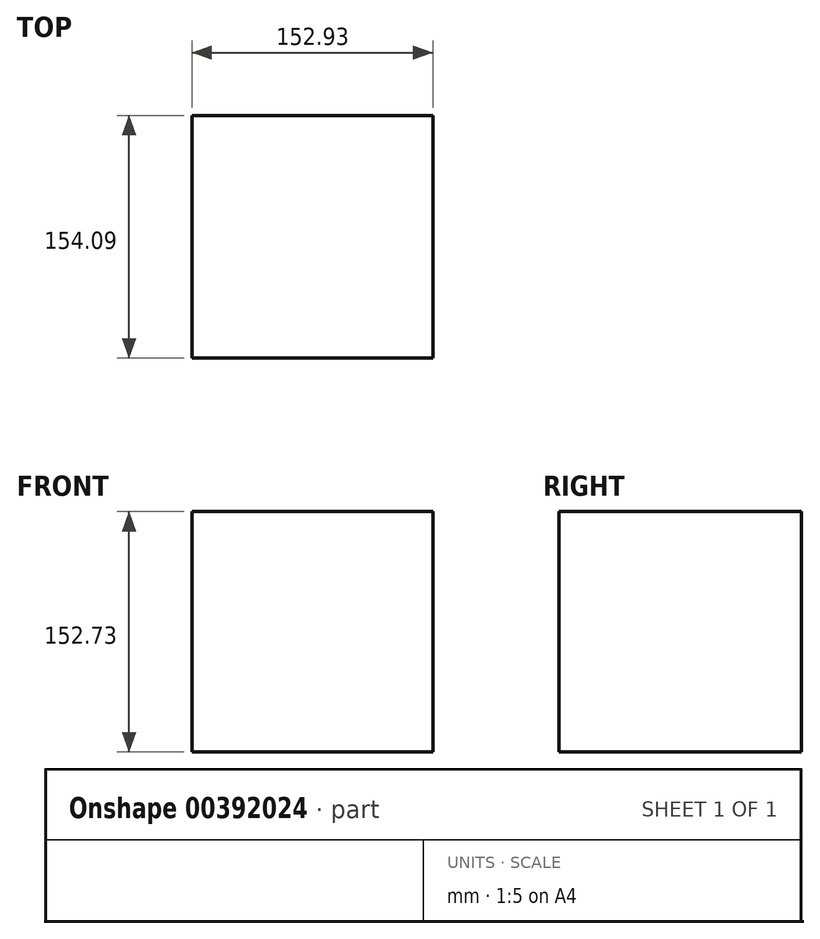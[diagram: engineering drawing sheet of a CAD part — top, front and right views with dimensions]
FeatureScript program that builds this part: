
annotation { "Feature Type Name" : "Feature", "Feature Type Description" : "" }
export const myFeature = defineFeature(function(context is Context, id is Id, definition is map)
    precondition{}
    {
        {
            var Q0;
            Q0=qCreatedBy(makeId("Front.planeOp"),FACE);
            var sketch = newSketch(context, id + "F0", { "sketchPlane" : qUnion([Q0])});
            skLineSegment(sketch, "E0.bottom", {"start": v(0, 0) * mm, "end": v(0, 0) * mm});
            skLineSegment(sketch, "E0.top", {"start": v(0, 0) * mm, "end": v(0, 0) * mm});
            skLineSegment(sketch, "E0.left", {"start": v(0, 0) * mm, "end": v(0, 0) * mm});
            skLineSegment(sketch, "E0.right", {"start": v(0, 0) * mm, "end": v(0, 0) * mm});
            skLineSegment(sketch, "E1.bottom", {"start": v(-77.16, -76.58) * mm, "end": v(75.77, -76.58) * mm});
            skLineSegment(sketch, "E1.top", {"start": v(-77.16, 76.15) * mm, "end": v(75.77, 76.15) * mm});
            skLineSegment(sketch, "E1.left", {"start": v(-77.16, -76.58) * mm, "end": v(-77.16, 76.15) * mm});
            skLineSegment(sketch, "E1.right", {"start": v(75.77, -76.58) * mm, "end": v(75.77, 76.15) * mm});
            skSolve(sketch);
        }
        {
            var Q0;
            Q0=makeQuery(id+"F0.imprint","IMPRINT",FACE,{"disambiguationData":[TD([[makeQuery(id+"F0.imprint","IMPRINT",EDGE,{"derivedFrom":sQuery(id+"F0.wireOp",EDGE,"E1.bottom")}),1.0]])]});
            extrude(context, id + "F1", {"entities" : qUnion([Q0]), "depth" : 25.4 * mm});
        }
        {
            var Q0;
            Q0=makeQuery(id+"F1.opExtrude","CAP_FACE",FACE,{"disambiguationData":[OSD([sQuery(id+"F0.wireOp",EDGE,"E1.bottom"),sQuery(id+"F0.wireOp",EDGE,"E1.top"),sQuery(id+"F0.wireOp",EDGE,"E1.left"),sQuery(id+"F0.wireOp",EDGE,"E1.right")])],"isStart":true});
            var Q1;
            Q1=makeQuery(id+"F1.opExtrude","CAP_FACE",FACE,{"disambiguationData":[OSD([sQuery(id+"F0.wireOp",EDGE,"E1.bottom"),sQuery(id+"F0.wireOp",EDGE,"E1.top"),sQuery(id+"F0.wireOp",EDGE,"E1.left"),sQuery(id+"F0.wireOp",EDGE,"E1.right")])],"isStart":false});
            extrude(context, id + "F2", {"entities" : qUnion([Q0, Q1]), "operationType" : NewBodyOperationType.ADD, "depth" : 75.1 * mm});
        }
        {
            var Q0;
            Q0=makeQuery(id+"F1.opExtrude","CAP_FACE",FACE,{"disambiguationData":[OSD([sQuery(id+"F0.wireOp",EDGE,"E1.bottom"),sQuery(id+"F0.wireOp",EDGE,"E1.top"),sQuery(id+"F0.wireOp",EDGE,"E1.left"),sQuery(id+"F0.wireOp",EDGE,"E1.right")])],"isStart":false});
            extrude(context, id + "F3", {"entities" : qUnion([Q0]), "operationType" : NewBodyOperationType.ADD, "depth" : 53.58 * mm});
        }
        {
            var Q0;
            {var subQ0=sQuery(id+"F0.wireOp",EDGE,"E1.left");Q0=makeQuery(id+"F3.boolean.opBoolean","MERGE",FACE,{"derivedFrom":[makeQuery(id+"F2.boolean.opBoolean","MERGE",FACE,{"derivedFrom":[makeQuery(id+"F1.opExtrude","SWEPT_FACE",FACE,{"disambiguationData":[OSD([subQ0])]}),makeQuery(id+"F2.opExtrude","SWEPT_FACE",FACE,{"disambiguationData":[OSD([subQ0]),TDD([makeQuery(id+"F1.opExtrude","CAP_EDGE",EDGE,{"disambiguationData":[OSD([subQ0])],"isStart":true})])]}),makeQuery(id+"F2.opExtrude","SWEPT_FACE",FACE,{"disambiguationData":[OSD([subQ0]),TDD([makeQuery(id+"F1.opExtrude","CAP_EDGE",EDGE,{"disambiguationData":[OSD([subQ0])],"isStart":false})])]})]}),makeQuery(id+"F3.opExtrude","SWEPT_FACE",FACE,{"disambiguationData":[OSD([subQ0])]})]});}
            extrude(context, id + "F4", {"entities" : qUnion([Q0]), "operationType" : NewBodyOperationType.ADD, "oppositeDirection" : true, "depth" : 25.4 * mm});
        }
    });
